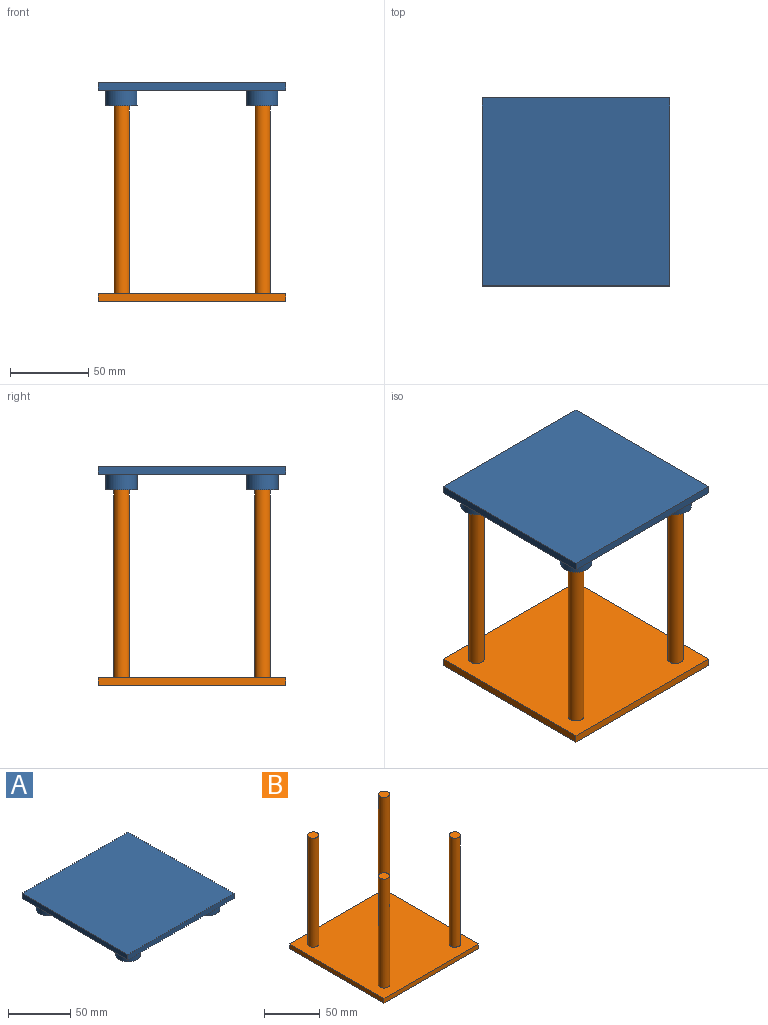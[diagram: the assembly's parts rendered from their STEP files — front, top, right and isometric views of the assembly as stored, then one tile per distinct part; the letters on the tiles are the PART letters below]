
ASSEMBLY  parts=2 mates=1
PART A: 22 faces, bbox 120x120x15 mm
  f0: plane 120x5mm, normal (0,1,0), area 600mm2, adj f1,f3,f4,f5
  f1: plane 120x5mm, normal (1,0,0), area 600mm2, adj f0,f2,f4,f5
  f2: plane 120x5mm, normal (0,-1,0), area 600mm2, adj f1,f3,f4,f5
  f3: plane 120x5mm, normal (-1,0,0), area 600mm2, adj f0,f2,f4,f5
  f4: plane 120x120mm, normal (0,0,-1), area 13143.4mm2, adj f0,f1,f2,f3,f7,f10,f14,f19
  f5: plane 120x120mm, normal (0,0,1), area 14400mm2, adj f0,f1,f2,f3
  f6: cylinder r=5.5mm len=11mm, axis (0,0,1), area 345.6mm2, adj f8,f9
  f7: cylinder r=10mm len=20mm, axis (0,0,1), area 628.3mm2, adj f4,f8
  f8: plane 20x20mm, normal (0,0,-1), area 219.1mm2, adj f6,f7
  f9: plane 11x11mm, normal (0,0,-1), area 95mm2, adj f6
  f10: cylinder r=10mm len=20mm, axis (0,0,1), area 628.3mm2, adj f4,f12
  f11: cylinder r=5.5mm len=11mm, axis (0,0,1), area 345.6mm2, adj f12,f13
  f12: plane 20x20mm, normal (0,0,-1), area 219.1mm2, adj f10,f11
  f13: plane 11x11mm, normal (0,0,-1), area 95mm2, adj f11
  f14: cylinder r=10mm len=20mm, axis (0,0,1), area 628.3mm2, adj f4,f16
  f15: cylinder r=5.5mm len=11mm, axis (0,0,1), area 345.6mm2, adj f16,f17
  f16: plane 20x20mm, normal (0,0,-1), area 219.1mm2, adj f14,f15
  f17: plane 11x11mm, normal (0,0,-1), area 95mm2, adj f15
  f18: cylinder r=5.5mm len=11mm, axis (0,0,1), area 345.6mm2, adj f20,f21
  f19: cylinder r=10mm len=20mm, axis (0,0,1), area 628.3mm2, adj f4,f20
  f20: plane 20x20mm, normal (0,0,-1), area 219.1mm2, adj f18,f19
  f21: plane 11x11mm, normal (0,0,-1), area 95mm2, adj f18
PART B: 14 faces, bbox 120x120x125 mm
  f0: plane 120x5mm, normal (0,-1,0), area 600mm2, adj f1,f3,f4,f5
  f1: plane 120x5mm, normal (1,0,0), area 600mm2, adj f0,f2,f4,f5
  f2: plane 120x5mm, normal (0,1,0), area 600mm2, adj f1,f3,f4,f5
  f3: plane 120x5mm, normal (-1,0,0), area 600mm2, adj f0,f2,f4,f5
  f4: plane 120x120mm, normal (0,0,1), area 14085.8mm2, adj f0,f1,f2,f3,f6,f8,f10,f12
  f5: plane 120x120mm, normal (0,0,-1), area 14400mm2, adj f0,f1,f2,f3
  f6: cylinder r=5mm len=120mm, axis (0,0,-1), area 3769.9mm2, adj f4,f7
  f7: plane 10x10mm, normal (0,0,1), area 78.5mm2, adj f6
  f8: cylinder r=5mm len=120mm, axis (0,0,-1), area 3769.9mm2, adj f4,f9
  f9: plane 10x10mm, normal (0,0,1), area 78.5mm2, adj f8
  f10: cylinder r=5mm len=120mm, axis (0,0,-1), area 3769.9mm2, adj f4,f11
  f11: plane 10x10mm, normal (0,0,1), area 78.5mm2, adj f10
  f12: cylinder r=5mm len=120mm, axis (0,0,-1), area 3769.9mm2, adj f4,f13
  f13: plane 10x10mm, normal (0,0,1), area 78.5mm2, adj f12
PLACE A t=(-136.35,17.5,166.52)mm
PLACE B t=(23.55,-31.04,26.52)mm
MATE fastened B.f6 <-> A.f6  axis (0,0,-1) through (-81.45,-16.04,151.52)mm
